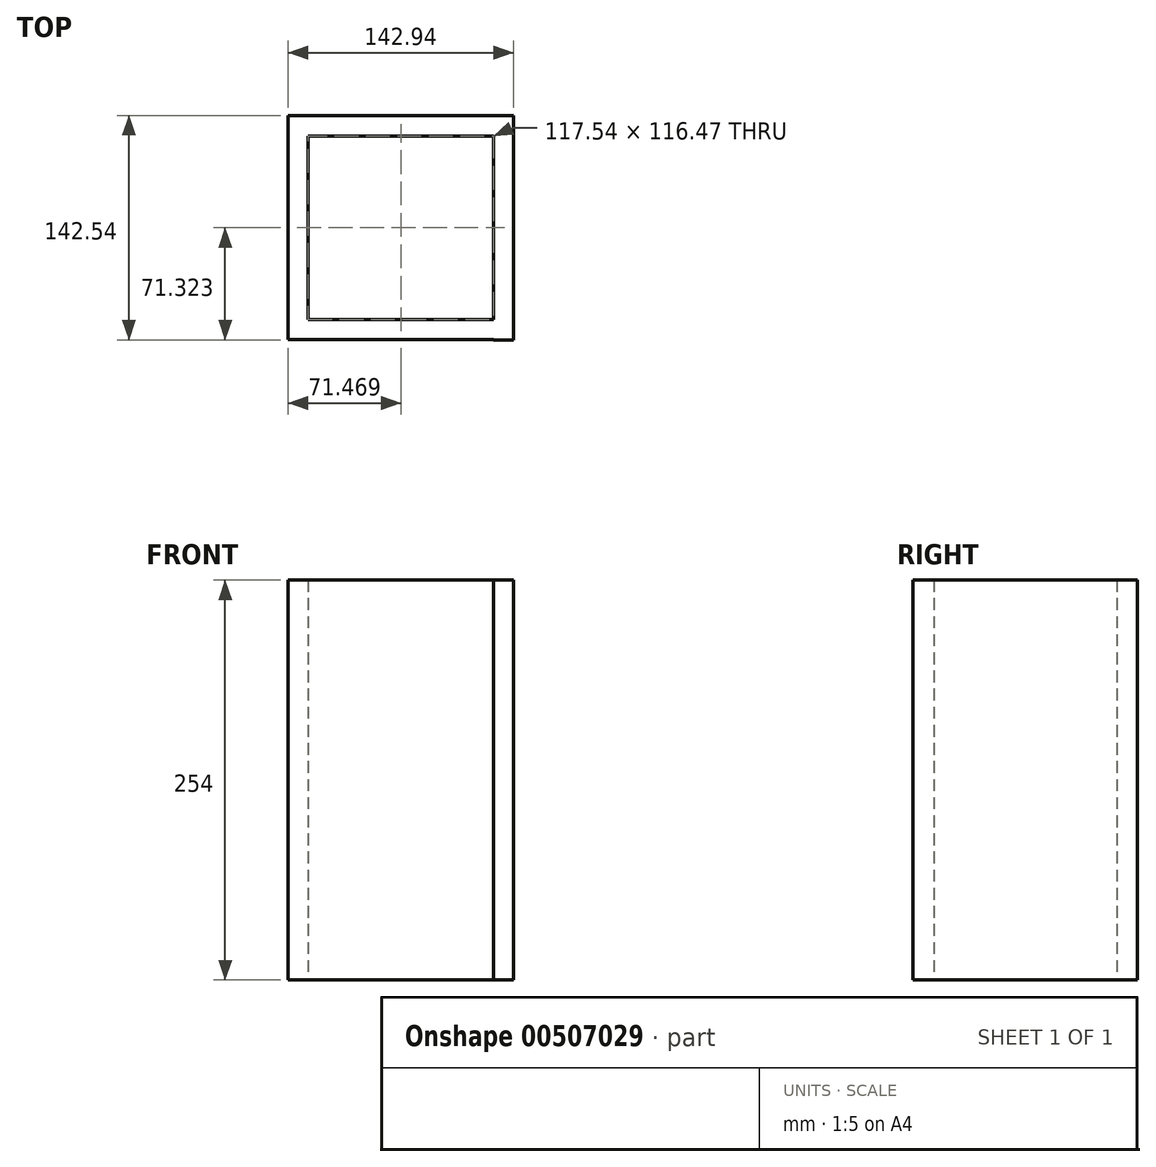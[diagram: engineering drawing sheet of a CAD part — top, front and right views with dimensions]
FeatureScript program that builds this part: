
annotation { "Feature Type Name" : "Feature", "Feature Type Description" : "" }
export const myFeature = defineFeature(function(context is Context, id is Id, definition is map)
    precondition{}
    {
        {
            var Q0;
            Q0=qCreatedBy(makeId("Top.planeOp"),FACE);
            var sketch = newSketch(context, id + "F0", { "sketchPlane" : qUnion([Q0])});
            skLineSegment(sketch, "E0.bottom", {"start": v(-71.8, -71.47) * mm, "end": v(-59.1, -71.47) * mm});
            skLineSegment(sketch, "E0.top", {"start": v(-71.8, 70.68) * mm, "end": v(-59.1, 70.68) * mm});
            skLineSegment(sketch, "E0.left", {"start": v(-71.8, -71.47) * mm, "end": v(-71.8, 70.68) * mm});
            skLineSegment(sketch, "E0.right", {"start": v(-59.1, -71.47) * mm, "end": v(-59.1, 70.68) * mm});
            skLineSegment(sketch, "E1.bottom", {"start": v(71.14, 70.68) * mm, "end": v(58.44, 70.68) * mm});
            skLineSegment(sketch, "E1.top", {"start": v(71.14, -71.86) * mm, "end": v(58.44, -71.86) * mm});
            skLineSegment(sketch, "E1.left", {"start": v(71.14, 70.68) * mm, "end": v(71.14, -71.86) * mm});
            skLineSegment(sketch, "E1.right", {"start": v(58.44, 70.68) * mm, "end": v(58.44, -71.86) * mm});
            skLineSegment(sketch, "E2.bottom", {"start": v(-59.1, -71.47) * mm, "end": v(58.44, -71.47) * mm});
            skLineSegment(sketch, "E2.top", {"start": v(-59.1, -58.77) * mm, "end": v(58.44, -58.77) * mm});
            skLineSegment(sketch, "E2.left", {"start": v(-59.1, -71.47) * mm, "end": v(-59.1, -58.77) * mm});
            skLineSegment(sketch, "E2.right", {"start": v(58.44, -71.47) * mm, "end": v(58.44, -58.77) * mm});
            skLineSegment(sketch, "E3.bottom", {"start": v(58.44, 70.68) * mm, "end": v(-59.1, 70.68) * mm});
            skLineSegment(sketch, "E3.top", {"start": v(58.44, 57.7) * mm, "end": v(-59.1, 57.7) * mm});
            skLineSegment(sketch, "E3.left", {"start": v(58.44, 70.68) * mm, "end": v(58.44, 57.7) * mm});
            skLineSegment(sketch, "E3.right", {"start": v(-59.1, 70.68) * mm, "end": v(-59.1, 57.7) * mm});
            skSolve(sketch);
        }
        {
            var Q0;
            Q0 = qSketchRegion(id + "F0", true);
            extrude(context, id + "F1", {"entities" : qUnion([Q0]), "depth" : 254 * mm});
        }
    });
